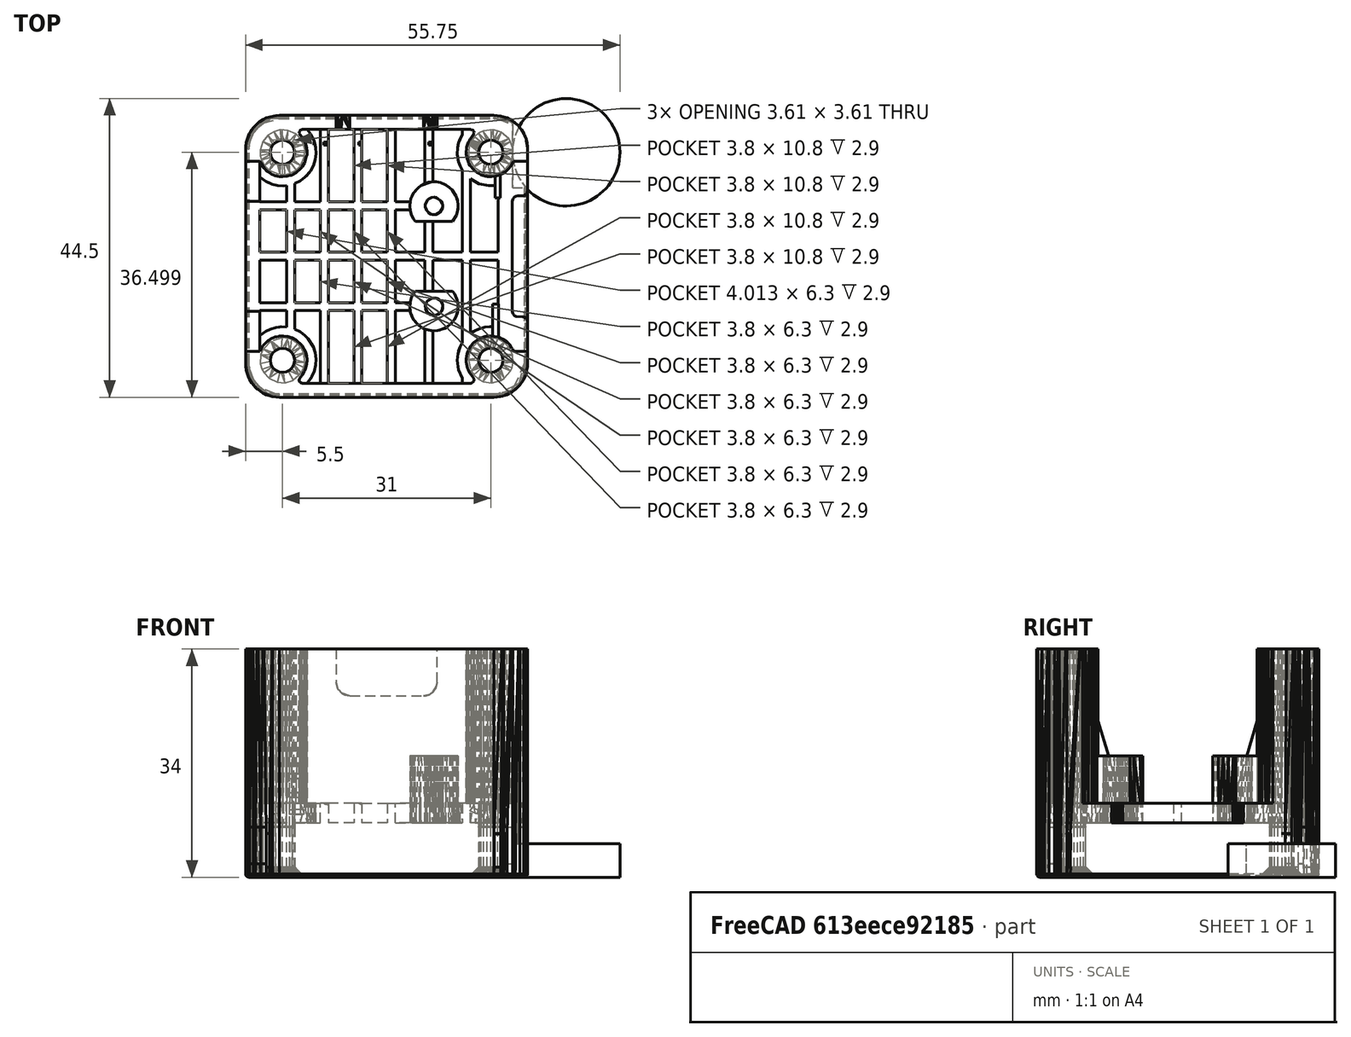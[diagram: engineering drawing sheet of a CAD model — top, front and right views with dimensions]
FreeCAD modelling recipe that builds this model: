
FCSTD DOCUMENT  (FreeCAD 0.18R16146 (Git))
Label: X Axis Endstop Cover
License: All rights reserved
LicenseURL: http://en.wikipedia.org/wiki/All_rights_reserved
objects: Part::Feature×1, Part::Cylinder×1, Part::Box×1, Part::Cut×1
note: 4 computed .brp shape members not serialized (recipe doc carries the construction recipe); baked Part::Feature solids carry a one-line shape summary decoded from their .brp

FEATURE [Part::Feature] Ender_3_X_axis_endstop_cover_V3001_solid001  label="Ender_3_X_axis_endstop_cover_V3001 (Solid)001"
  shape: bbox 42 x 42 x 34 mm, 2941 faces (baked)
FEATURE [Part::Cylinder] Cylinder
  Angle = 360
  AttacherType = Attacher::AttachEngine3D
  Height = 5
  Placement = pos=(24.25,17,0) rot=(0,0,1;0rad)
  Radius = 8
FEATURE [Part::Box] Box  label="Cube"
  AttacherType = Attacher::AttachEngine3D
  Height = 5
  Length = 10
  Placement = pos=(16.25,11.75,0) rot=(0,0,1;0rad)
  Width = 10
FEATURE [Part::Cut] Cut
  Base = -> Ender_3_X_axis_endstop_cover_V3001_solid001
  Tool = -> Box
